FCSTD DOCUMENT  (FreeCAD 1.0R39109 (Git))
Label: Metal_Sheet_Cutout
License: All rights reserved
LicenseURL: https://en.wikipedia.org/wiki/All_rights_reserved
objects: Part::Feature×30, Part::Cylinder×8, Part::Cut×6, Sketcher::SketchObject×6, Part::Extrusion×6, Part::FeaturePython×4, App::Part×4, Part::Fillet×3, Part::Cone×2, Part::Box×1, Part::MultiFuse×1, Part::Compound×1
note: 74 computed .brp shape members not serialized (recipe doc carries the construction recipe); baked Part::Feature solids carry a one-line shape summary decoded from their .brp

FEATURE [Part::Box] Box  label="Base"
  AttacherType = Attacher::AttachEngine3D
  Height = 593
  Length = 470
  Placement = pos=(-235,0,0) rot=(0,0,1;0rad)
  Width = 4
FEATURE [Part::Feature] Part__Feature  label="15275A57_Corner Bracket"
  Placement = pos=(-210,0,592.5) rot=(0,0.707107,0.707107;3.14159rad)
  shape: bbox 50.01 x 54.99 x 45.01 mm, 103 faces (baked)
FEATURE [Part::FeaturePython] Clone  label="tSlotTop"  # WARN: FeaturePython — macro-defined, semantics opaque (R4)
  AttacherType = Attacher::AttachEngine3D
  Fuse = false
  Placement = pos=(0,-49.4,554) rot=(1,0,0;1.5708rad)
  Scale = (1,1,3)
FEATURE [Part::FeaturePython] Clone001  label="tSlotBottom"  # WARN: FeaturePython — macro-defined, semantics opaque (R4)
  AttacherType = Attacher::AttachEngine3D
  Fuse = false
  Placement = pos=(0,-49.4,38) rot=(1,0,0;1.5708rad)
  Scale = (1,1,3)
FEATURE [Part::Cone] Cone002  label="base009"
  Angle = 360
  AttacherType = Attacher::AttachEngine3D
  Height = 9
  Placement = pos=(0,0,-12.5) rot=(0,0,1;0rad)
  Radius1 = 14.5
  Radius2 = 12.5
FEATURE [Part::Cone] Cone003  label="base010"
  Angle = 360
  AttacherType = Attacher::AttachEngine3D
  Height = 3.5
  Placement = pos=(0,0,-3.5) rot=(0,0,1;0rad)
  Radius1 = 12.5
  Radius2 = 9.94
FEATURE [Part::Cylinder] Cylinder208
  Angle = 360
  AttacherType = Attacher::AttachEngine3D
  FirstAngle = 0
  Height = 10
  Placement = pos=(0,-8,-36.5) rot=(1,0,0;1.5708rad)
  Radius = 3.75
  SecondAngle = 0
FEATURE [Part::Cylinder] Cylinder209  label="antenna001"
  Angle = 360
  AttacherType = Attacher::AttachEngine3D
  FirstAngle = 0
  Height = 1100
  Radius = 9.935
  SecondAngle = 0
FEATURE [Part::Cylinder] Cylinder210  label="antennaTip001"
  Angle = 360
  AttacherType = Attacher::AttachEngine3D
  FirstAngle = 0
  Height = 25
  Placement = pos=(0,0,1100) rot=(0,0,1;0rad)
  Radius = 10.785
  SecondAngle = 0
FEATURE [Part::Cylinder] Cylinder211  label="Base004"
  Angle = 360
  AttacherType = Attacher::AttachEngine3D
  FirstAngle = 0
  Height = 29
  Placement = pos=(0,0,-41.5) rot=(0,0,1;0rad)
  Radius = 14.5
  SecondAngle = 0
FEATURE [Part::Cylinder] Cylinder212  label="base012"
  Angle = 360
  AttacherType = Attacher::AttachEngine3D
  FirstAngle = 0
  Height = 10
  Placement = pos=(0,0,-51.5) rot=(0,0,1;0rad)
  Radius = 10
  SecondAngle = 0
FEATURE [Part::Cylinder] Cylinder213  label="base013"
  Angle = 360
  AttacherType = Attacher::AttachEngine3D
  FirstAngle = 0
  Height = 1.5
  Placement = pos=(0,0,-53) rot=(0,0,1;0rad)
  Radius = 9
  SecondAngle = 0
FEATURE [Part::Cylinder] Cylinder214
  Angle = 360
  AttacherType = Attacher::AttachEngine3D
  FirstAngle = 0
  Height = 10.3
  Placement = pos=(0,0,-84.8) rot=(0,0,1;0rad)
  Radius = 12
  SecondAngle = 0
FEATURE [Part::Cylinder] Cylinder215
  Angle = 360
  AttacherType = Attacher::AttachEngine3D
  FirstAngle = 0
  Height = 10
  Placement = pos=(0,-8,-36.5) rot=(1,0,0;1.5708rad)
  Radius = 3.75
  SecondAngle = 0
FEATURE [Part::Cut] Cut152  label="base011"
  Base = -> Cylinder211
  Refine = true
  Tool = -> Cylinder215
FEATURE [Part::Feature] Part__Feature340  label="SOLID004"
  Placement = pos=(0,0,0) rot=(1,0,0;1.5708rad)
  shape: bbox 24 x 24 x 23 mm, 53 faces (baked)
FEATURE [Part::Cut] Cut151  label="LoraPlug001"
  Base = -> Part__Feature340
  Placement = pos=(0,0,32) rot=(0,0,1;0rad)
  Refine = true
  Tool = -> Cylinder214
FEATURE [Sketcher::SketchObject] Sketch401
  ArcFitTolerance = 1e-06
  FullyConstrained = true
  MakeInternals = false
  Placement = pos=(0,0,0) rot=(1,0,0;1.5708rad)
  sketch-geometry (9):
    g0: LineSegment StartX=175 StartY=593 StartZ=0 EndX=235 EndY=593 EndZ=0
    g1: LineSegment StartX=235 StartY=593 StartZ=0 EndX=235 EndY=333 EndZ=0
    g2: LineSegment StartX=235 StartY=333 StartZ=0 EndX=185 EndY=333 EndZ=0
    g3: LineSegment StartX=185 StartY=333 StartZ=0 EndX=185 EndY=498 EndZ=0
    g4: LineSegment StartX=185 StartY=498 StartZ=0 EndX=175 EndY=508 EndZ=0
    g5: LineSegment StartX=175 StartY=508 StartZ=0 EndX=175 EndY=593 EndZ=0
    g6: Circle CenterX=182.5 CenterY=573 CenterZ=0 NormalX=0 NormalY=0 NormalZ=1 AngleXU=0 Radius=2.125
    g7: Circle CenterX=182.5 CenterY=553 CenterZ=0 NormalX=0 NormalY=0 NormalZ=1 AngleXU=0 Radius=2.125
    g8: Circle CenterX=182.5 CenterY=533 CenterZ=0 NormalX=0 NormalY=0 NormalZ=1 AngleXU=0 Radius=2.125
  constraints (27):
    c: Horizontal(g0)
    c: Coincident(g1,g0)
    c: Vertical(g1)
    c: Coincident(g2,g1)
    c: Horizontal(g2)
    c: Coincident(g3,g2)
    c: Vertical(g3)
    c: Coincident(g5,g4)
    c: Vertical(g5)
    c: Coincident(g3,g4)
    c: Coincident(g0,g5)
    c: DistanceX(g2,g2) = 50
    c: DistanceX(g1) = 235
    c: DistanceY(g0) = 593
    c: DistanceX(g0,g0) = 60
    c: DistanceY(g5,g5) = 85
    c: Angle(g4) = 2.35619
    c: DistanceY(g1,g1) = 260
    c: Equal(g6,g7)
    c: Equal(g6,g8)
    c: Diameter(g6) = 4.25
    c: Vertical(g8,g7)
    c: Vertical(g7,g6)
    c: DistanceY(g6,g0) = 20
    c: DistanceY(g7,g6) = 20
    c: DistanceY(g8,g7) = 20
    c: DistanceX(g0,g6) = 7.5
FEATURE [Part::Extrusion] Extrude172
  Base = -> Sketch401
  Dir = (0,-1,2e-16)
  DirMode = 2
  FaceMakerClass = Part::FaceMakerBullseye
  FaceMakerMode = 3
  LengthFwd = 6
  LengthRev = 0
  Solid = true
  Symmetric = false
FEATURE [Sketcher::SketchObject] Sketch402
  ArcFitTolerance = 1e-06
  FullyConstrained = true
  MakeInternals = false
  Placement = pos=(0,0,333) rot=(0,0,1;0rad)
  sketch-geometry (5):
    g0: LineSegment StartX=235 StartY=0 StartZ=0 EndX=235 EndY=-20 EndZ=0
    g1: LineSegment StartX=195 StartY=0 StartZ=0 EndX=195 EndY=-20 EndZ=0
    g2: ArcOfCircle CenterX=215 CenterY=-20 CenterZ=0 NormalX=0 NormalY=0 NormalZ=1 AngleXU=0 Radius=20 StartAngle=3.14159 EndAngle=6.28319
    g3: Circle CenterX=215 CenterY=-20 CenterZ=0 NormalX=0 NormalY=0 NormalZ=1 AngleXU=0 Radius=16.25
    g4: LineSegment StartX=195 StartY=0 StartZ=0 EndX=235 EndY=0 EndZ=0
  constraints (15):
    c: Vertical(g0)
    c: Vertical(g1)
    c: Coincident(g2,g1)
    c: Coincident(g2,g0)
    c: DistanceY(g1) = 0
    c: Coincident(g3,g2)
    c: Diameter(g3) = 32.5
    c: Horizontal(g2,g0)
    c: Horizontal(g0,g1)
    c: DistanceX(g2) = 215
    c: DistanceY(g2) = -20
    c: Horizontal(g0,g1)
    c: DistanceX(g0) = 235
    c: Coincident(g4,g1)
    c: Coincident(g4,g0)
FEATURE [Part::Extrusion] Extrude173
  Base = -> Sketch402
  Dir = (0,0,1)
  DirMode = 2
  FaceMakerClass = Part::FaceMakerBullseye
  FaceMakerMode = 3
  LengthFwd = 260
  LengthRev = 0
  Solid = true
  Symmetric = false
FEATURE [Sketcher::SketchObject] Sketch403
  ArcFitTolerance = 1e-06
  FullyConstrained = true
  MakeInternals = false
  Placement = pos=(0,0,333) rot=(0,0,1;0rad)
  sketch-geometry (5):
    g0: LineSegment StartX=235 StartY=0 StartZ=0 EndX=235 EndY=-20 EndZ=0
    g1: LineSegment StartX=195 StartY=0 StartZ=0 EndX=195 EndY=-20 EndZ=0
    g2: ArcOfCircle CenterX=215 CenterY=-20 CenterZ=0 NormalX=0 NormalY=0 NormalZ=1 AngleXU=0 Radius=20 StartAngle=3.14159 EndAngle=6.28319
    g3: Circle CenterX=215 CenterY=-20 CenterZ=0 NormalX=0 NormalY=0 NormalZ=1 AngleXU=0 Radius=12.5
    g4: LineSegment StartX=195 StartY=0 StartZ=0 EndX=235 EndY=0 EndZ=0
  constraints (15):
    c: Vertical(g0)
    c: Vertical(g1)
    c: Coincident(g2,g1)
    c: Coincident(g2,g0)
    c: DistanceY(g1) = 0
    c: Coincident(g3,g2)
    c: Diameter(g3) = 25
    c: Horizontal(g2,g0)
    c: Horizontal(g0,g1)
    c: DistanceX(g2) = 215
    c: DistanceY(g2) = -20
    c: Horizontal(g0,g1)
    c: DistanceX(g0) = 235
    c: Coincident(g4,g1)
    c: Coincident(g4,g0)
FEATURE [Part::Extrusion] Extrude174
  Base = -> Sketch403
  Dir = (0,0,1)
  DirMode = 2
  FaceMakerClass = Part::FaceMakerBullseye
  FaceMakerMode = 3
  LengthFwd = 10
  LengthRev = 0
  Solid = true
  Symmetric = false
FEATURE [Part::MultiFuse] Fusion183  label="antennaHolder001"
  Shapes = -> [Extrude172,Extrude173,Extrude174]
FEATURE [Part::Fillet] Fillet264
  Base = -> Fusion183
  EdgeLinks = -> Fusion183 [Edge24]
  Edges = 1 edges r=8: [Edge24]
FEATURE [Sketcher::SketchObject] Sketch404
  ArcFitTolerance = 1e-06
  FullyConstrained = true
  MakeInternals = false
  Placement = pos=(0,0,343) rot=(0,0,1;0rad)
  sketch-geometry (1):
    g0: Circle CenterX=215 CenterY=-20 CenterZ=0 NormalX=0 NormalY=0 NormalZ=1 AngleXU=0 Radius=16.25
  constraints (3):
    c: Diameter(g0) = 32.5
    c: DistanceX(g0) = 215
    c: DistanceY(g0) = -20
FEATURE [Part::Extrusion] Extrude175
  Base = -> Sketch404
  Dir = (0,0,1)
  DirMode = 2
  FaceMakerClass = Part::FaceMakerBullseye
  FaceMakerMode = 3
  LengthFwd = 260
  LengthRev = 0
  Solid = true
  Symmetric = false
FEATURE [Part::Cut] Cut153  label="antennaHolder002"
  Base = -> Fillet264
  Tool = -> Extrude175
FEATURE [Part::Fillet] Fillet265  label="antennaHolder003"
  Base = -> Cut153
  EdgeLinks = -> Cut153 [Edge8,Edge10,Edge11,Edge17,Edge55,Edge65]
  Edges = 6 edges: [Edge8 r=1,Edge10 r=1,Edge11 r=3,Edge17 r=3,Edge55 r=1,Edge65 r=3]
FEATURE [Sketcher::SketchObject] Sketch405
  ArcFitTolerance = 1e-06
  FullyConstrained = true
  MakeInternals = false
  Placement = pos=(0,-19.5,0) rot=(1,0,0;1.5708rad)
  sketch-geometry (4):
    g0: ArcOfCircle CenterX=215 CenterY=583.5 CenterZ=0 NormalX=0 NormalY=0 NormalZ=1 AngleXU=0 Radius=8 StartAngle=3.14159 EndAngle=6.28319
    g1: LineSegment StartX=207 StartY=583.5 StartZ=0 EndX=207 EndY=593 EndZ=0
    g2: LineSegment StartX=207 StartY=593 StartZ=0 EndX=223 EndY=593 EndZ=0
    g3: LineSegment StartX=223 StartY=593 StartZ=0 EndX=223 EndY=583.5 EndZ=0
  constraints (13):
    c: Coincident(g1,g0)
    c: Vertical(g1)
    c: Coincident(g2,g1)
    c: Horizontal(g2)
    c: Coincident(g3,g2)
    c: Coincident(g3,g0)
    c: Vertical(g3)
    c: Horizontal(g0,g0)
    c: Horizontal(g0,g0)
    c: DistanceX(g0) = 215
    c: DistanceY(g0) = 583.5
    c: Diameter(g0) = 16
    c: DistanceY(g1) = 593
FEATURE [Part::Extrusion] Extrude176
  Base = -> Sketch405
  Dir = (0,-1,2e-16)
  DirMode = 2
  FaceMakerClass = Part::FaceMakerBullseye
  FaceMakerMode = 3
  LengthFwd = 25
  LengthRev = 0
  Solid = true
  Symmetric = false
FEATURE [Part::Cut] Cut154  label="antennaHolder004"
  Base = -> Fillet265
  Tool = -> Extrude176
FEATURE [Part::Fillet] Fillet266  label="antennaHolder005"
  Base = -> Cut154
  EdgeLinks = -> Cut154 [Edge40,Edge41,Edge91,Edge92,Edge93,Edge143]
  Edges = 6 edges r=1: [Edge40,Edge41,Edge91,Edge92,Edge93,Edge143]
FEATURE [Part::FeaturePython] Tube006  # WARN: FeaturePython — macro-defined, semantics opaque (R4)
  AttacherType = Attacher::AttachEngine3D
  Height = 250
  InnerRadius = 14.7
  OuterRadius = 16
  Placement = pos=(0,0,-277) rot=(0,0,1;0rad)
FEATURE [Part::Cut] Cut150  label="metalHolder "
  Base = -> Tube006
  Placement = pos=(215,-20,620) rot=(0,0,1;0rad)
  Refine = true
  Tool = -> Cylinder208
FEATURE [Part::FeaturePython] Tube007  label="BaseOuter001"  # WARN: FeaturePython — macro-defined, semantics opaque (R4)
  AttacherType = Attacher::AttachEngine3D
  Height = 10
  InnerRadius = 14.5
  OuterRadius = 17.25
  Placement = pos=(0,0,-26.5) rot=(0,0,1;0rad)
FEATURE [App::Part] Part004  label="Antenna001"
  Group = -> [Cylinder209,Cylinder210,Cone002,Cone003,Cylinder212,Cylinder213,Cylinder214,Part__Feature340,Cut151,Cylinder211,Cylinder215,Cut152,Tube007]
  Origin = -> Origin010
  Placement = pos=(215,-19.5,620) rot=(0,0,1;0rad)
FEATURE [Part::Compound] Compound002  label="loraAntennaAndMounts"
  Links = -> [Fillet266,Part004,Cut150]
FEATURE [Part::Feature] Part__Feature016  label="Z_-16147B_ZH-16147B-01"
  shape: bbox 438.9 x 219.4 x 405.1 mm, 3210 faces (baked)
FEATURE [Part::Feature] Part__Feature017  label="INSERTS-4"
  Placement = pos=(-180.975,-168.256,-155.575) rot=(0,0,1;0rad)
  shape: bbox 7.519 x 8.463 x 7.519 mm, 71 faces (baked)
FEATURE [Part::Feature] Part__Feature018  label="INSERTS-005"
  Placement = pos=(-170.872,-174.835,-145.472) rot=(0,0,1;3.14159rad)
  shape: bbox 7.519 x 8.463 x 7.519 mm, 71 faces (baked)
FEATURE [Part::Feature] Part__Feature019  label="INSERTS-006"
  Placement = pos=(-205.994,-3.7592,-180.594) rot=(0,0,1;3.14159rad)
  shape: bbox 7.519 x 8.463 x 7.519 mm, 71 faces (baked)
FEATURE [Part::Feature] Part__Feature020  label="INSERTS-007"
  Placement = pos=(-180.975,-168.083,155.575) rot=(1,0,0;3.14159rad)
  shape: bbox 7.519 x 8.463 x 7.519 mm, 71 faces (baked)
FEATURE [Part::Feature] Part__Feature021  label="INSERTS-008"
  Placement = pos=(-170.872,-175.008,145.472) rot=(0,1,0;3.14159rad)
  shape: bbox 7.519 x 8.463 x 7.519 mm, 71 faces (baked)
FEATURE [Part::Feature] Part__Feature022  label="INSERTS-009"
  Placement = pos=(-205.994,-3.93217,180.594) rot=(0,1,0;3.14159rad)
  shape: bbox 7.519 x 8.463 x 7.519 mm, 71 faces (baked)
FEATURE [Part::Feature] Part__Feature023  label="INSERTS-010"
  Placement = pos=(180.975,-168.083,-155.575) rot=(0,0,1;3.14159rad)
  shape: bbox 7.519 x 8.463 x 7.519 mm, 71 faces (baked)
FEATURE [Part::Feature] Part__Feature024  label="INSERTS-011"
  Placement = pos=(170.872,-175.008,-145.472) rot=(0,0,1;0rad)
  shape: bbox 7.519 x 8.463 x 7.519 mm, 71 faces (baked)
FEATURE [Part::Feature] Part__Feature025  label="INSERTS-012"
  Placement = pos=(205.994,-3.93217,-180.594) rot=(0,0,1;0rad)
  shape: bbox 7.519 x 8.463 x 7.519 mm, 71 faces (baked)
FEATURE [Part::Feature] Part__Feature026  label="INSERTS-013"
  Placement = pos=(180.975,-168.256,155.575) rot=(0,1,0;3.14159rad)
  shape: bbox 7.519 x 8.463 x 7.519 mm, 71 faces (baked)
FEATURE [Part::Feature] Part__Feature027  label="INSERTS-014"
  Placement = pos=(170.872,-174.835,145.472) rot=(1,0,0;3.14159rad)
  shape: bbox 7.519 x 8.463 x 7.519 mm, 71 faces (baked)
FEATURE [Part::Feature] Part__Feature028  label="INSERTS-015"
  Placement = pos=(205.994,-3.7592,180.594) rot=(1,0,0;3.14159rad)
  shape: bbox 7.519 x 8.463 x 7.519 mm, 71 faces (baked)
FEATURE [Part::Feature] Part__Feature029  label="LABEL-104"
  Placement = pos=(-1.221e-12,-20.3197,-180.67) rot=(1,0,0;1.56207rad)
  shape: bbox 63.5 x 38.1 x 0.3833 mm, 10 faces (baked)
FEATURE [Part::Feature] Part__Feature030  label="Z_-16141C_ZH-16141C-01"
  shape: bbox 448.9 x 49.63 x 409 mm, 1738 faces (baked)
FEATURE [Part::Feature] Part__Feature031  label="ZH-1614G"
  Placement = pos=(0,0.635,6.9e-15) rot=(0,0,1;0rad)
  shape: bbox 434.5 x 6.35 x 383.7 mm, 136 faces (baked)
FEATURE [Part::Feature] Part__Feature032  label="ZH-01F_ZH-01F-01"
  Placement = pos=(-158.172,-191.294,-145.472) rot=(0,0,1;0rad)
  shape: bbox 75.05 x 15.88 x 54.71 mm, 393 faces (baked)
FEATURE [Part::Feature] Part__Feature033  label="pan cross head_ai_SCREWS-046"
  Placement = pos=(-170.872,-191.294,-145.472) rot=(-0.002139,-0.002139,0.999995;1.5708rad)
  shape: bbox 10.25 x 22.43 x 10.25 mm, 92 faces (baked)
FEATURE [Part::Feature] Part__Feature034  label="pan cross head_ai_SCREWS-047"
  Placement = pos=(-170.872,-191.294,145.472) rot=(0.002139,0.002139,0.999995;1.5708rad)
  shape: bbox 10.25 x 22.43 x 10.25 mm, 92 faces (baked)
FEATURE [Part::Feature] Part__Feature035  label="ZH-01F_ZH-01F-002"
  Placement = pos=(-158.172,-191.294,145.472) rot=(0,0,1;0rad)
  shape: bbox 75.05 x 15.88 x 54.71 mm, 393 faces (baked)
FEATURE [Part::Feature] Part__Feature036  label="pan cross head_ai_SCREWS-048"
  Placement = pos=(170.872,-191.294,-145.472) rot=(0.707106,0.707106,-0.001512;3.14462rad)
  shape: bbox 10.25 x 22.43 x 10.25 mm, 92 faces (baked)
FEATURE [Part::Feature] Part__Feature037  label="pan cross head_ai_SCREWS-049"
  Placement = pos=(170.872,-191.294,145.472) rot=(0.707106,0.707106,0.001512;3.13857rad)
  shape: bbox 10.25 x 22.43 x 10.25 mm, 92 faces (baked)
FEATURE [Part::Feature] Part__Feature038  label="ZH-01F_ZH-01F-003"
  Placement = pos=(158.172,-191.294,-145.472) rot=(0,1,0;3.14159rad)
  shape: bbox 75.05 x 15.88 x 54.71 mm, 393 faces (baked)
FEATURE [Part::Feature] Part__Feature039  label="ZH-01F_ZH-01F-004"
  Placement = pos=(158.172,-191.294,145.472) rot=(0,1,0;3.14159rad)
  shape: bbox 75.05 x 15.88 x 54.71 mm, 393 faces (baked)
FEATURE [Part::Feature] Part__Feature040  label="SCREWS-047_default"
  Placement = pos=(-205.994,12.0142,-180.594) rot=(-1,0,0;1.5708rad)
  shape: bbox 9.234 x 22.51 x 9.177 mm, 32 faces (baked)
FEATURE [Part::Feature] Part__Feature041  label="SCREWS-047_default001"
  Placement = pos=(205.994,12.0142,-180.594) rot=(-1,0,0;1.5708rad)
  shape: bbox 9.234 x 22.51 x 9.177 mm, 32 faces (baked)
FEATURE [Part::Feature] Part__Feature042  label="SCREWS-047_default002"
  Placement = pos=(-205.994,12.0142,180.594) rot=(-1,0,0;1.5708rad)
  shape: bbox 9.234 x 22.51 x 9.177 mm, 32 faces (baked)
FEATURE [Part::Feature] Part__Feature043  label="SCREWS-047_default003"
  Placement = pos=(205.994,12.0142,180.594) rot=(-1,0,0;1.5708rad)
  shape: bbox 9.234 x 22.51 x 9.177 mm, 32 faces (baked)
FEATURE [App::Part] Z__16141CG_ZH_16141CG_01  label="Z_-16141CG_ZH-16141CG-01"
  Group = -> [Part__Feature030,Part__Feature031]
  Origin = -> Origin005
FEATURE [App::Part] Z__16147BI_ZH_16147BI_01  label="Z_-16147BI_ZH-16147BI-01"
  Group = -> [Part__Feature016,Part__Feature017,Part__Feature018,Part__Feature019,Part__Feature020,Part__Feature021,Part__Feature022,Part__Feature023,Part__Feature024,Part__Feature025,Part__Feature026,Part__Feature027,Part__Feature028,Part__Feature029]
  Origin = -> Origin004
FEATURE [App::Part] ZH_161407_33  label="ZH-161407-33"
  Group = -> [Z__16147BI_ZH_16147BI_01,Z__16141CG_ZH_16141CG_01,Part__Feature032,Part__Feature033,Part__Feature034,Part__Feature035,Part__Feature036,Part__Feature037,Part__Feature038,Part__Feature039,Part__Feature040,Part__Feature041,Part__Feature042,Part__Feature043]
  Origin = -> Origin006
  Placement = pos=(0,-180,296) rot=(0.707107,0,0.707107;3.14159rad)
FEATURE [Sketcher::SketchObject] Sketch
  ArcFitTolerance = 1e-06
  FullyConstrained = true
  MakeInternals = false
  Placement = pos=(0,0,0) rot=(1,0,0;1.5708rad)
  sketch-geometry (17):
    g0: Circle CenterX=-225.865 CenterY=576.71 CenterZ=0 NormalX=0 NormalY=0 NormalZ=1 AngleXU=0 Radius=2
    g1: Circle CenterX=-225.865 CenterY=569.71 CenterZ=0 NormalX=0 NormalY=0 NormalZ=1 AngleXU=0 Radius=2
    g2: Circle CenterX=-225.865 CenterY=559.56 CenterZ=0 NormalX=0 NormalY=0 NormalZ=1 AngleXU=0 Radius=2
    g3: Circle CenterX=-210 CenterY=556.6 CenterZ=0 NormalX=0 NormalY=0 NormalZ=1 AngleXU=0 Radius=2
    g4: Circle CenterX=-210 CenterY=578.1 CenterZ=0 NormalX=0 NormalY=0 NormalZ=1 AngleXU=0 Radius=2
    g5: Circle CenterX=-194.115 CenterY=576.71 CenterZ=0 NormalX=0 NormalY=0 NormalZ=1 AngleXU=0 Radius=2
    g6: Circle CenterX=-194.115 CenterY=569.71 CenterZ=0 NormalX=0 NormalY=0 NormalZ=1 AngleXU=0 Radius=2
    g7: Circle CenterX=-194.115 CenterY=559.56 CenterZ=0 NormalX=0 NormalY=0 NormalZ=1 AngleXU=0 Radius=2
    g8: Circle CenterX=0 CenterY=38 CenterZ=0 NormalX=0 NormalY=0 NormalZ=1 AngleXU=0 Radius=3
    g9: Circle CenterX=0 CenterY=554 CenterZ=0 NormalX=0 NormalY=0 NormalZ=1 AngleXU=0 Radius=3
    g10: Circle CenterX=182.5 CenterY=573 CenterZ=0 NormalX=0 NormalY=0 NormalZ=1 AngleXU=0 Radius=2
    g11: Circle CenterX=182.5 CenterY=553 CenterZ=0 NormalX=0 NormalY=0 NormalZ=1 AngleXU=0 Radius=2
    g12: Circle CenterX=182.5 CenterY=533 CenterZ=0 NormalX=0 NormalY=0 NormalZ=1 AngleXU=0 Radius=2
    g13: Circle CenterX=145.475 CenterY=466.9 CenterZ=0 NormalX=0 NormalY=0 NormalZ=1 AngleXU=0 Radius=2.5
    g14: Circle CenterX=-145.475 CenterY=466.9 CenterZ=0 NormalX=0 NormalY=0 NormalZ=1 AngleXU=0 Radius=2.5
    g15: Circle CenterX=-145.475 CenterY=125.1 CenterZ=0 NormalX=0 NormalY=0 NormalZ=1 AngleXU=0 Radius=2.5
    g16: Circle CenterX=145.475 CenterY=125.1 CenterZ=0 NormalX=0 NormalY=0 NormalZ=1 AngleXU=0 Radius=2.5
  constraints (45):
    c: PointOnObject(g8,g-2)
    c: PointOnObject(g9,g-2)
    c: Equal(g0, g1-g7) x7
    c: Diameter(g0) = 4
    c: Distance(g0,g-2) = 225.865
    c: Distance(g0,g-1) = 576.71
    c: Vertical(g1,g2)
    c: Horizontal(g0,g5)
    c: DistanceX(g0,g5) = 31.75
    c: DistanceY(g1,g0) = 7
    c: DistanceX(g1,g6) = 31.75
    c: DistanceX(g2,g7) = 31.75
    c: DistanceY(g2,g1) = 10.15
    c: Horizontal(g1,g6)
    c: Horizontal(g2,g7)
    c: Vertical(g6,g5)
    c: Distance(g4,g-2) = 210
    c: Distance(g4,g-1) = 578.1
    c: Vertical(g4,g3)
    c: DistanceY(g3,g4) = 21.5
    c: Distance(g9,g-1) = 554
    c: DistanceY(g8,g9) = 516
    c: Equal(g8,g9)
    c: Diameter(g8) = 6
    c: Distance(g10,g-2) = 182.5
    c: Distance(g10,g-1) = 573
    c: Vertical(g10,g11)
    c: Vertical(g10,g12)
    c: DistanceY(g11,g10) = 20
    c: DistanceY(g12,g11) = 20
    c: Equal(g10,g11)
    c: Equal(g10,g12)
    c: Diameter(g10) = 4
    c: Distance(g13,g-2) = 145.475
    c: DistanceY(g-1,g13) = 466.9
    c: Horizontal(g13,g14)
    c: Distance(g14,g-2) = 145.475
    c: Vertical(g14,g15)
    c: Vertical(g13,g16)
    c: DistanceY(g15,g14) = 341.8
    c: Horizontal(g15,g16)
    c: Equal(g13,g14)
    c: Equal(g13,g15)
    c: Equal(g13,g16)
    c: Diameter(g13) = 5
FEATURE [Part::Extrusion] Extrude
  Base = -> Sketch
  Dir = (0,-1,2e-16)
  DirMode = 2
  FaceMakerClass = Part::FaceMakerBullseye
  FaceMakerMode = 3
  LengthFwd = 20
  LengthRev = 0
  Placement = pos=(0,13,0) rot=(0,0,1;0rad)
  Solid = true
  Symmetric = false
FEATURE [Part::Cut] Cut  label="Base_HoleCut"
  Base = -> Box
  Placement = pos=(0,0,0) rot=(1,0,0;4.71239rad)
  Refine = true
  Tool = -> Extrude
